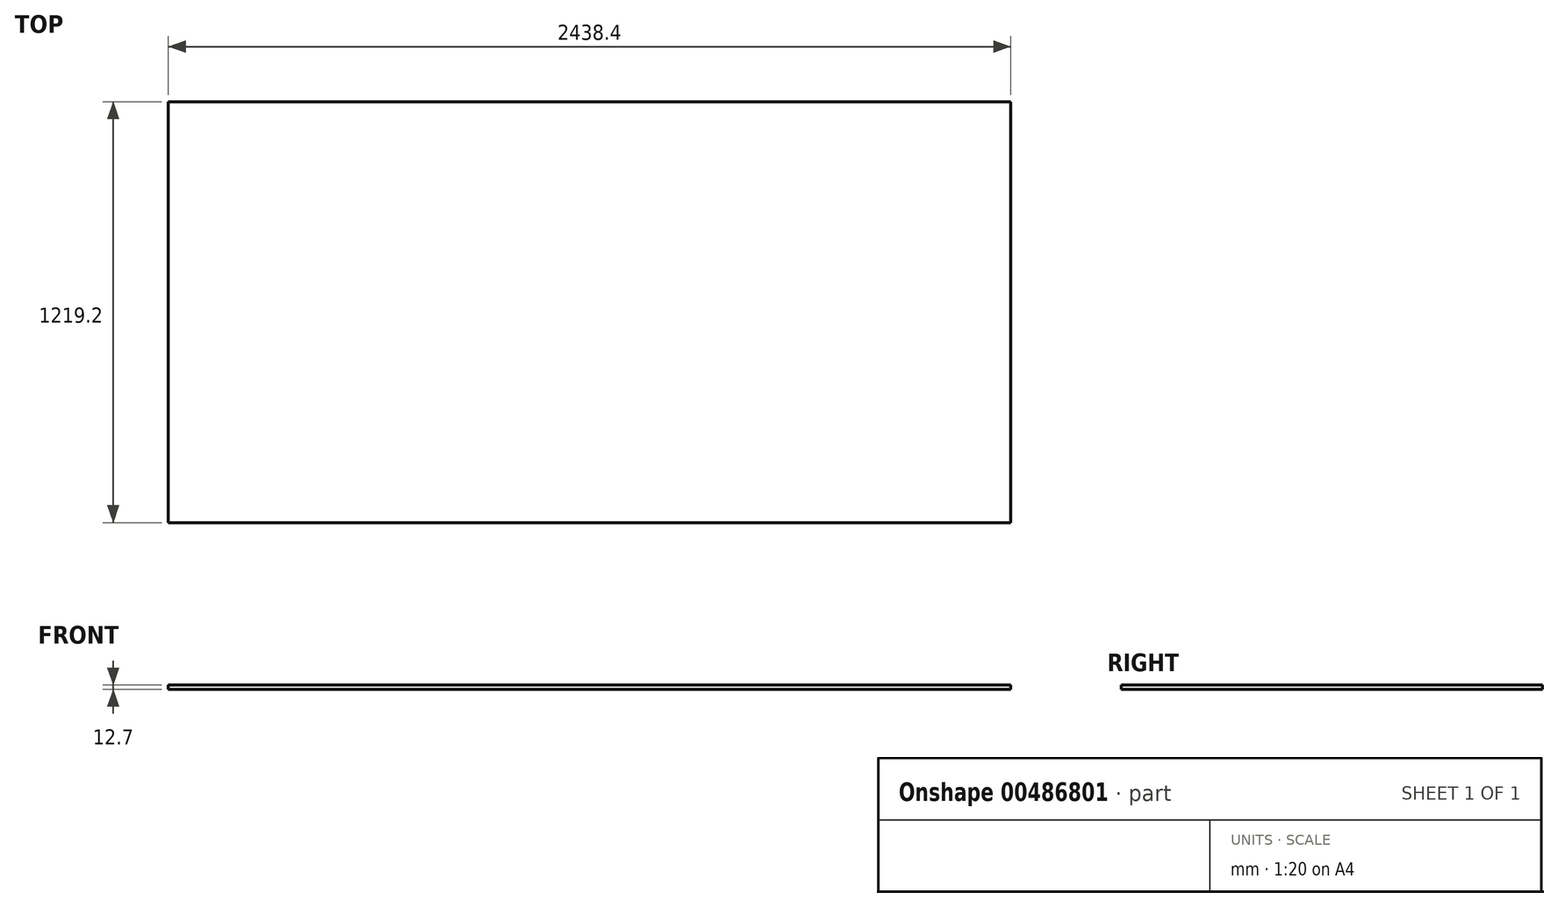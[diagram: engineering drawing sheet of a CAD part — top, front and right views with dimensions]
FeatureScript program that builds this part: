
annotation { "Feature Type Name" : "Feature", "Feature Type Description" : "" }
export const myFeature = defineFeature(function(context is Context, id is Id, definition is map)
    precondition{}
    {
        {
            var Q0;
            Q0=qCreatedBy(makeId("Top.planeOp"),FACE);
            var sketch = newSketch(context, id + "F0", { "sketchPlane" : qUnion([Q0])});
            skLineSegment(sketch, "E0.bottom", {"start": v(-1219.2, 609.6) * mm, "end": v(1219.2, 609.6) * mm});
            skLineSegment(sketch, "E0.top", {"start": v(-1219.2, -609.6) * mm, "end": v(1219.2, -609.6) * mm});
            skLineSegment(sketch, "E0.left", {"start": v(1219.2, -609.6) * mm, "end": v(1219.2, 609.6) * mm});
            skLineSegment(sketch, "E0.right", {"start": v(-1219.2, -609.6) * mm, "end": v(-1219.2, 609.6) * mm});
            skPoint(sketch, "E0.middle", {"position": v(0, 0) * mm});
            skSolve(sketch);
        }
        {
            var Q0;
            Q0=makeQuery(id+"F0.imprint","IMPRINT",FACE,{"disambiguationData":[TD([[makeQuery(id+"F0.imprint","IMPRINT",EDGE,{"derivedFrom":sQuery(id+"F0.wireOp",EDGE,"E0.bottom")}),-1.0]])]});
            extrude(context, id + "F1", {"entities" : qUnion([Q0]), "depth" : 12.7 * mm});
        }
    });
